# Revit family: Trane_TVR_Indoor_Floor standing_4TVN0018(24,27)EF000AA(2nd DC)
name_source: partatom
category: Equipamento mecânico
units: mm (PartAtom-declared; Revit-internal decimal feet)

## family parameters
Com base no plano de trabalho = Não
Compartilhado = Não
Corte com vazios quando carregada = Não
Cota do conector redondo = Utilizar diâmetro
Número OmniClass = 23.75.00.00
Ponto de cálculo do ambiente = Não
Sempre na vertical = Sim
Tipo de parte = Normal
Título OmniClass = Climate Control (HVAC)

## types (3) — shared parameters
Condensation = air
Depth = 220  [stored 0.721785 ft]
Descrição = High efficiency air cooled
Fabricante = Trane
Gas = R410a
Gas pipe = 15.9  [stored 0.0521654 ft]
Height = 596  [stored 1.95538 ft]
Installation = Indoor installation
Liquid pipe = 9.53
MCA (Minimum Circuit Amps) = 15 A
MFA (Maximum Fuse Amps) = 1 A
Machine material = Galvanized Steel
Panel color = S1004
Power supply = 220-240V ~50Hz
Series = TVR ULTRA
URL = https://www.trane.com
Width = 1500  [stored 4.92126 ft]

## per-type parameters (varying)
| type | Air  Flow | Cooling Capacity | Cooling Power Input | Heating Capacity | Heating Power Input | Net Weight |
| 4TVN0018EF000AA | 1150/1094/1028/970/925/886/830 m3/h | 6 kW | 88 W | 6 kW | 88 W | 40.00 kg |
| 4TVN0024EF000AA | 1380/1290/1205/1100/1033/955/870m3/h | 7 kW | 110 W | 8 kW | 110 W | 40.00 kg |
| 4TVN0027EF000AA | 1380/1290/1205/1100/1033/955/870 m3/h | 8 kW | 130 W | 9 kW | 130 W | 41.50 kg |

note: column(s) folded — value = type name in every type: Modelo

note: [stored X ft] marks values corroborated as IEEE doubles in the binary element streams (Revit-internal decimal feet)
